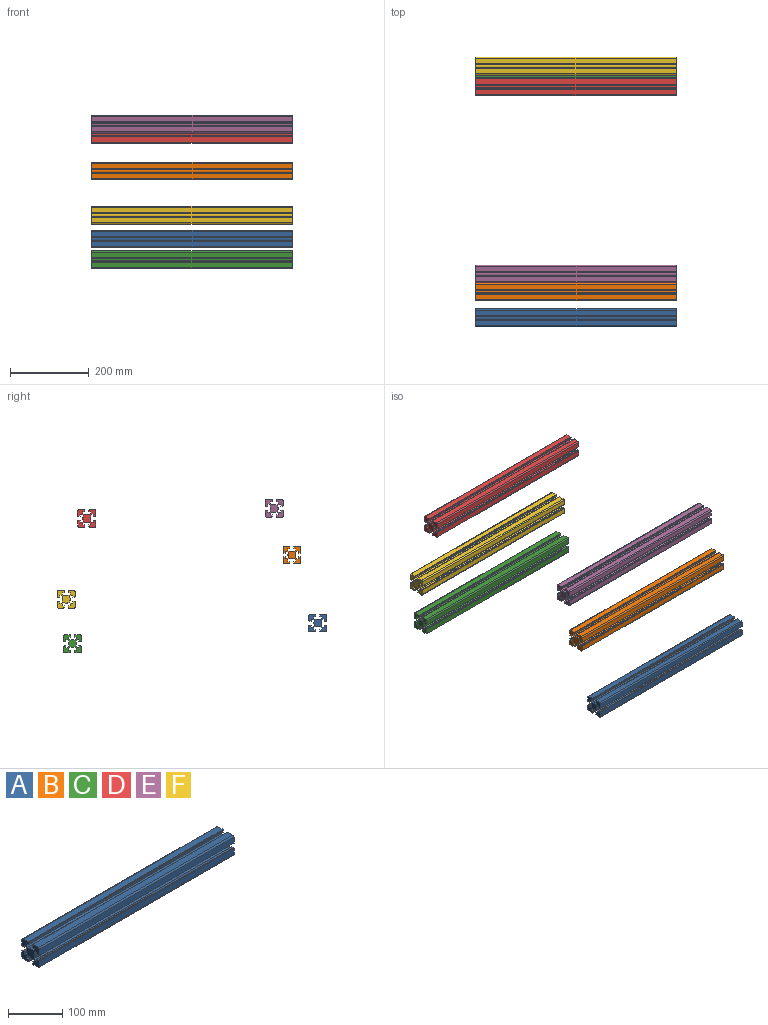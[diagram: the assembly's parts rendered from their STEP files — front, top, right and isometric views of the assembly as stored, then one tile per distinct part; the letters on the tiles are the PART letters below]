
ASSEMBLY  parts=6 mates=5
PART A: 98 faces, bbox 508x45x45 mm
  f0: plane 508x4.03mm, normal (0,-1,0), area 2049.4mm2, adj f1,f95,f96,f97
  f1: plane 508x2.89mm, normal (0,-0.71,0.71), area 2078.3mm2, adj f0,f2,f96,f97
  f2: plane 508x4.11mm, normal (0,0,1), area 2086.4mm2, adj f1,f3,f96,f97
  f3: plane 508x4.75mm, normal (0,1,0), area 2413.1mm2, adj f2,f4,f96,f97
  f4: cylinder r=0.3mm len=508mm, axis (-1,0,0), area 239.4mm2, adj f3,f5,f96,f97
  f5: plane 508x3.9mm, normal (0,0,1), area 1981.2mm2, adj f4,f6,f96,f97
  f6: cylinder r=0.3mm len=508mm, axis (-1,0,0), area 239.4mm2, adj f5,f7,f96,f97
  f7: plane 508x0.5mm, normal (0,-1,0), area 254mm2, adj f6,f8,f96,f97
  f8: plane 508x1.2mm, normal (0,0,1), area 609.7mm2, adj f7,f9,f96,f97
  f9: cylinder r=0.3mm len=508mm, axis (-1,0,0), area 239.4mm2, adj f8,f10,f96,f97
  f10: plane 508x13.4mm, normal (0,-1,0), area 6807.3mm2, adj f9,f11,f96,f97
  f11: cylinder r=3mm len=508mm, axis (-1,0,0), area 2393.9mm2, adj f10,f12,f96,f97
  f12: plane 508x13.4mm, normal (0,0,-1), area 6807.2mm2, adj f11,f13,f96,f97
  f13: cylinder r=0.3mm len=508mm, axis (-1,0,0), area 239.4mm2, adj f12,f14,f96,f97
  f14: plane 508x1.2mm, normal (0,1,0), area 609.7mm2, adj f13,f15,f96,f97
  f15: plane 508x0.5mm, normal (0,0,-1), area 254mm2, adj f14,f16,f96,f97
  f16: cylinder r=0.3mm len=508mm, axis (-1,0,0), area 239.4mm2, adj f15,f17,f96,f97
  f17: plane 508x3.9mm, normal (0,1,0), area 1981.2mm2, adj f16,f18,f96,f97
  f18: cylinder r=0.3mm len=508mm, axis (-1,0,0), area 239.4mm2, adj f17,f19,f96,f97
  f19: plane 508x4.75mm, normal (0,0,1), area 2413.1mm2, adj f18,f20,f96,f97
  f20: plane 508x4.11mm, normal (0,1,0), area 2086.4mm2, adj f19,f21,f96,f97
  f21: plane 508x2.89mm, normal (0,0.71,-0.71), area 2078.3mm2, adj f20,f22,f96,f97
  f22: plane 508x4.03mm, normal (0,0,-1), area 2049.4mm2, adj f21,f23,f96,f97
  f23: cylinder r=10mm len=508mm, axis (-1,0,0), area 3226.9mm2, adj f22,f24,f96,f97
  f24: plane 508x4.03mm, normal (0,0,-1), area 2049.4mm2, adj f23,f25,f96,f97
  f25: plane 508x2.89mm, normal (0,-0.71,-0.71), area 2078.3mm2, adj f24,f26,f96,f97
  f26: plane 508x4.11mm, normal (0,-1,0), area 2086.4mm2, adj f25,f27,f96,f97
  f27: plane 508x4.75mm, normal (0,0,1), area 2413.1mm2, adj f26,f28,f96,f97
  f28: cylinder r=0.3mm len=508mm, axis (-1,0,0), area 239.4mm2, adj f27,f29,f96,f97
  f29: plane 508x3.9mm, normal (0,-1,0), area 1981.2mm2, adj f28,f30,f96,f97
  f30: cylinder r=0.3mm len=508mm, axis (-1,0,0), area 239.4mm2, adj f29,f31,f96,f97
  f31: plane 508x0.5mm, normal (0,0,-1), area 254mm2, adj f30,f32,f96,f97
  f32: plane 508x1.2mm, normal (0,-1,0), area 609.7mm2, adj f31,f33,f96,f97
  f33: cylinder r=0.3mm len=508mm, axis (-1,0,0), area 239.4mm2, adj f32,f34,f96,f97
  f34: plane 508x13.4mm, normal (0,0,-1), area 6807.2mm2, adj f33,f35,f96,f97
  f35: cylinder r=3mm len=508mm, axis (-1,0,0), area 2393.9mm2, adj f34,f36,f96,f97
  f36: plane 508x13.4mm, normal (0,1,0), area 6807.3mm2, adj f35,f37,f96,f97
  f37: cylinder r=0.3mm len=508mm, axis (-1,0,0), area 239.4mm2, adj f36,f38,f96,f97
  f38: plane 508x1.2mm, normal (0,0,1), area 609.7mm2, adj f37,f39,f96,f97
  f39: plane 508x0.5mm, normal (0,1,0), area 254mm2, adj f38,f40,f96,f97
  f40: cylinder r=0.3mm len=508mm, axis (-1,0,0), area 239.4mm2, adj f39,f41,f96,f97
  f41: plane 508x3.9mm, normal (0,0,1), area 1981.2mm2, adj f40,f42,f96,f97
  f42: cylinder r=0.3mm len=508mm, axis (-1,0,0), area 239.4mm2, adj f41,f43,f96,f97
  f43: plane 508x4.75mm, normal (0,-1,0), area 2413.1mm2, adj f42,f44,f96,f97
  f44: plane 508x4.11mm, normal (0,0,1), area 2086.4mm2, adj f43,f45,f96,f97
  f45: plane 508x2.89mm, normal (0,0.71,0.71), area 2078.3mm2, adj f44,f46,f96,f97
  f46: plane 508x4.03mm, normal (0,1,0), area 2049.4mm2, adj f45,f47,f96,f97
  f47: cylinder r=10mm len=508mm, axis (-1,0,0), area 3226.9mm2, adj f46,f48,f96,f97
  f48: plane 508x4.03mm, normal (0,1,0), area 2049.4mm2, adj f47,f49,f96,f97
  f49: plane 508x2.89mm, normal (0,0.71,-0.71), area 2078.3mm2, adj f48,f50,f96,f97
  f50: plane 508x4.11mm, normal (0,0,-1), area 2086.4mm2, adj f49,f51,f96,f97
  f51: plane 508x4.75mm, normal (0,-1,0), area 2413.1mm2, adj f50,f52,f96,f97
  f52: cylinder r=0.3mm len=508mm, axis (-1,0,0), area 239.4mm2, adj f51,f53,f96,f97
  f53: plane 508x3.9mm, normal (0,0,-1), area 1981.2mm2, adj f52,f54,f96,f97
  f54: cylinder r=0.3mm len=508mm, axis (-1,0,0), area 239.4mm2, adj f53,f55,f96,f97
  f55: plane 508x0.5mm, normal (0,1,0), area 254mm2, adj f54,f56,f96,f97
  f56: plane 508x1.2mm, normal (0,0,-1), area 609.7mm2, adj f55,f57,f96,f97
  f57: cylinder r=0.3mm len=508mm, axis (-1,0,0), area 239.4mm2, adj f56,f58,f96,f97
  f58: plane 508x13.4mm, normal (0,1,0), area 6807.3mm2, adj f57,f59,f96,f97
  f59: cylinder r=3mm len=508mm, axis (-1,0,0), area 2393.9mm2, adj f58,f60,f96,f97
  f60: plane 508x13.4mm, normal (0,0,1), area 6807.2mm2, adj f59,f61,f96,f97
  f61: cylinder r=0.3mm len=508mm, axis (-1,0,0), area 239.4mm2, adj f60,f62,f96,f97
  f62: plane 508x1.2mm, normal (0,-1,0), area 609.7mm2, adj f61,f63,f96,f97
  f63: plane 508x0.5mm, normal (0,0,1), area 254mm2, adj f62,f64,f96,f97
  f64: cylinder r=0.3mm len=508mm, axis (-1,0,0), area 239.4mm2, adj f63,f65,f96,f97
  f65: plane 508x3.9mm, normal (0,-1,0), area 1981.2mm2, adj f64,f66,f96,f97
  f66: cylinder r=0.3mm len=508mm, axis (-1,0,0), area 239.4mm2, adj f65,f67,f96,f97
  f67: plane 508x4.75mm, normal (0,0,-1), area 2413.1mm2, adj f66,f68,f96,f97
  f68: plane 508x4.11mm, normal (0,-1,0), area 2086.4mm2, adj f67,f69,f96,f97
  f69: plane 508x2.89mm, normal (0,-0.71,0.71), area 2078.3mm2, adj f68,f70,f96,f97
  f70: plane 508x4.03mm, normal (0,0,1), area 2049.4mm2, adj f69,f71,f96,f97
  f71: cylinder r=10mm len=508mm, axis (-1,0,0), area 3226.9mm2, adj f70,f72,f96,f97
  f72: plane 508x4.03mm, normal (0,0,1), area 2049.4mm2, adj f71,f73,f96,f97
  f73: plane 508x2.89mm, normal (0,0.71,0.71), area 2078.3mm2, adj f72,f74,f96,f97
  f74: plane 508x4.11mm, normal (0,1,0), area 2086.4mm2, adj f73,f75,f96,f97
  f75: plane 508x4.75mm, normal (0,0,-1), area 2413.1mm2, adj f74,f76,f96,f97
  f76: cylinder r=0.3mm len=508mm, axis (-1,0,0), area 239.4mm2, adj f75,f77,f96,f97
  f77: plane 508x3.9mm, normal (0,1,0), area 1981.2mm2, adj f76,f78,f96,f97
  f78: cylinder r=0.3mm len=508mm, axis (-1,0,0), area 239.4mm2, adj f77,f79,f96,f97
  f79: plane 508x0.5mm, normal (0,0,1), area 254mm2, adj f78,f80,f96,f97
  f80: plane 508x1.2mm, normal (0,1,0), area 609.7mm2, adj f79,f81,f96,f97
  f81: cylinder r=0.3mm len=508mm, axis (-1,0,0), area 239.4mm2, adj f80,f82,f96,f97
  f82: plane 508x13.4mm, normal (0,0,1), area 6807.2mm2, adj f81,f83,f96,f97
  f83: cylinder r=3mm len=508mm, axis (-1,0,0), area 2393.9mm2, adj f82,f84,f96,f97
  f84: plane 508x13.4mm, normal (0,-1,0), area 6807.3mm2, adj f83,f85,f96,f97
  f85: cylinder r=0.3mm len=508mm, axis (-1,0,0), area 239.4mm2, adj f84,f86,f96,f97
  f86: plane 508x1.2mm, normal (0,0,-1), area 609.7mm2, adj f85,f87,f96,f97
  f87: plane 508x0.5mm, normal (0,-1,0), area 254mm2, adj f86,f88,f96,f97
  f88: cylinder r=0.3mm len=508mm, axis (-1,0,0), area 239.4mm2, adj f87,f89,f96,f97
  f89: plane 508x3.9mm, normal (0,0,-1), area 1981.2mm2, adj f88,f90,f96,f97
  f90: cylinder r=0.3mm len=508mm, axis (-1,0,0), area 239.4mm2, adj f89,f91,f96,f97
  f91: plane 508x4.75mm, normal (0,1,0), area 2413.1mm2, adj f90,f92,f96,f97
  f92: plane 508x4.11mm, normal (0,0,-1), area 2086.4mm2, adj f91,f93,f96,f97
  f93: plane 508x2.89mm, normal (0,-0.71,-0.71), area 2078.3mm2, adj f92,f94,f96,f97
  f94: plane 508x4.03mm, normal (0,-1,0), area 2049.4mm2, adj f93,f95,f96,f97
  f95: cylinder r=10mm len=508mm, axis (-1,0,0), area 3226.9mm2, adj f0,f94,f96,f97
  f96: plane 45x45mm, normal (1,0,0), area 1246.3mm2, adj f0,f1,f2,f3,f4,f5,f6,f7
  f97: plane 45x45mm, normal (-1,0,0), area 1246.3mm2, adj f0,f1,f2,f3,f4,f5,f6,f7
PART B: same geometry as A
PART C: same geometry as A
PART D: same geometry as A
PART E: same geometry as A
PART F: same geometry as A
PLACE A t=(-555.91,-260.91,85.36)mm
PLACE B t=(-555.91,-195.07,258.02)mm
PLACE C t=(-555.91,361.74,32.86)mm
PLACE D t=(-555.91,325.31,351.03)mm
PLACE E t=(-555.91,-150.29,376.7)mm
PLACE F t=(-555.91,377.73,145.86)mm
MATE planar B.f47 <-> E.f47  axis (1,0,0) through (-47.91,-194.16,253.54)mm
MATE planar F.f47 <-> C.f47  axis (1,0,0) through (-47.91,378.64,141.37)mm
MATE planar A.f47 <-> B.f47  axis (1,0,0) through (-47.91,-260,80.87)mm
MATE planar D.f47 <-> C.f47  axis (1,0,0) through (-47.91,326.22,346.54)mm
MATE planar C.f47 <-> B.f47  axis (1,0,0) through (-47.91,362.65,28.37)mm
